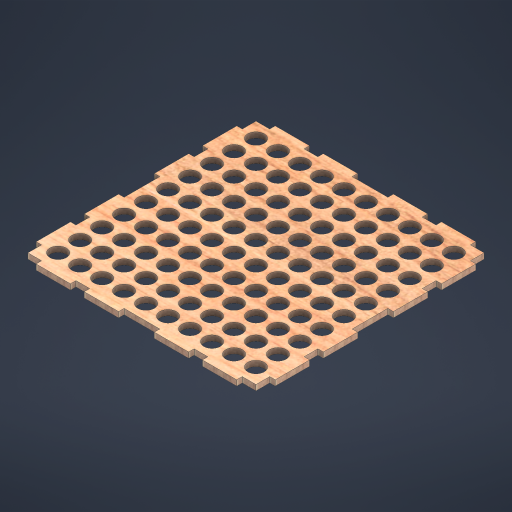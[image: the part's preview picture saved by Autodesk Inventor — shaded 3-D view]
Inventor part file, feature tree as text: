
AUTODESK INVENTOR PART (.ipt)
format: ipt  version: 2024.1 (Build 281209000, 209)  size: 666,624 bytes
history: native  units: mm
features: extrude x1, sketch x1
ambient origin geometry x8: Origin, YZ Plane, XZ Plane, XY Plane, X Axis, Y Axis, Z Axis, Center Point
bodies: Solid1 (feature_tree)
feature tree (2):
  extrude  "Extrusion1"  Depth=100.0mm
  sketch  "Sketch1"  dims[d0=12.0mm d1=100.0mm d3=16.0mm d4=100.0mm d6=16.0mm d9=5.0mm d10=5.0mm d11=4.0mm d12=4.0mm d13=10.0mm d14=10.0mm d15=25.0mm d16=4.0mm d17=25.0mm d18=10.0mm d19=25.0mm d20=10.0mm d21=25.0mm d22=4.0mm d23=40.0mm d25=360.0deg d27=4.0mm d28=0.0mm]
